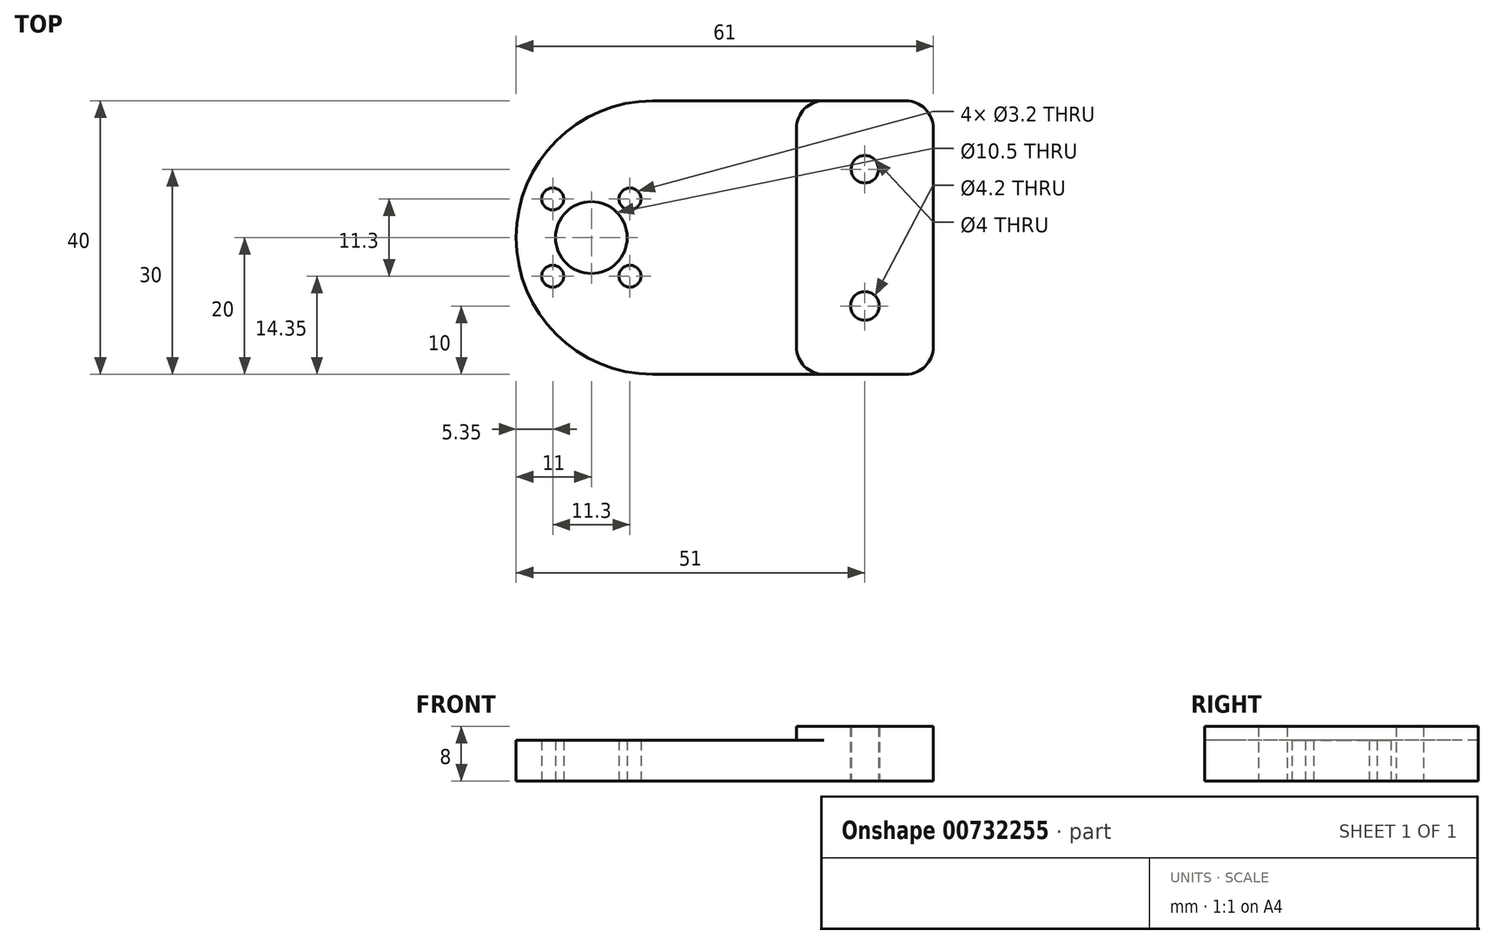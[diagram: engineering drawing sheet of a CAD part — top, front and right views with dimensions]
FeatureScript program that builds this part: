
annotation { "Feature Type Name" : "Feature", "Feature Type Description" : "" }
export const myFeature = defineFeature(function(context is Context, id is Id, definition is map)
    precondition{}
    {
        {
            var Q0;
            Q0=qCreatedBy(makeId("Top.planeOp"),FACE);
            var sketch = newSketch(context, id + "F0", { "sketchPlane" : qUnion([Q0])});
            skLineSegment(sketch, "E0.bottom", {"start": v(30.5, -20) * mm, "end": v(-30.5, -20) * mm});
            skLineSegment(sketch, "E0.top", {"start": v(30.5, 20) * mm, "end": v(-30.5, 20) * mm});
            skLineSegment(sketch, "E0.left", {"start": v(30.5, -20) * mm, "end": v(30.5, 20) * mm});
            skLineSegment(sketch, "E0.right", {"start": v(-30.5, -20) * mm, "end": v(-30.5, 20) * mm});
            skPoint(sketch, "E0.middle", {"position": v(0, 0) * mm});
            skCircle(sketch, "E1", {"center": v(-19.5, 0) * mm, "radius": 5.25 * mm});
            skLineSegment(sketch, "E2.bottom", {"start": v(-13.85, -5.65) * mm, "end": v(-25.15, -5.65) * mm, "construction": true});
            skLineSegment(sketch, "E2.top", {"start": v(-13.85, 5.65) * mm, "end": v(-25.15, 5.65) * mm, "construction": true});
            skLineSegment(sketch, "E2.left", {"start": v(-13.85, -5.65) * mm, "end": v(-13.85, 5.65) * mm, "construction": true});
            skLineSegment(sketch, "E2.right", {"start": v(-25.15, -5.65) * mm, "end": v(-25.15, 5.65) * mm, "construction": true});
            skCircle(sketch, "E3", {"center": v(-13.85, 5.65) * mm, "radius": 1.6 * mm});
            skCircle(sketch, "E4", {"center": v(-25.15, 5.65) * mm, "radius": 1.6 * mm});
            skCircle(sketch, "E5", {"center": v(-13.85, -5.65) * mm, "radius": 1.6 * mm});
            skCircle(sketch, "E6", {"center": v(-25.15, -5.65) * mm, "radius": 1.6 * mm});
            skCircle(sketch, "E7", {"center": v(20.5, -10) * mm, "radius": 2.1 * mm});
            skCircle(sketch, "E8", {"center": v(20.5, 10) * mm, "radius": 2 * mm});
            skSolve(sketch);
        }
        {
            var Q0;
            Q0=qSketchRegion(id+"F0",true);
            extrude(context, id + "F1", {"entities" : qUnion([Q0]), "depth" : 6 * mm, "offsetDistance" : 25 * mm});
        }
        {
            var Q0;
            Q0=qSketchRegion(id+"F0",true);
            extrude(context, id + "F2", {"entities" : qUnion([Q0]), "operationType" : NewBodyOperationType.REMOVE, "endBound" : BoundingType.THROUGH_ALL, "oppositeDirection" : true, "depth" : 25 * mm, "offsetDistance" : 25 * mm});
        }
        {
            var Q0;
            Q0=makeQuery(id+"F1.opExtrude","SWEPT_EDGE",EDGE,{"disambiguationData":[OSD([sQuery(id+"F0.wireOp",EDGE,"E0.bottom"),sQuery(id+"F0.wireOp",EDGE,"E0.right")])]});
            var Q1;
            Q1=makeQuery(id+"F1.opExtrude","SWEPT_EDGE",EDGE,{"disambiguationData":[OSD([sQuery(id+"F0.wireOp",EDGE,"E0.top"),sQuery(id+"F0.wireOp",EDGE,"E0.right")])]});
            fillet(context, id + "F3", {"entities" : qUnion([Q0, Q1]), "radius" : 20 * mm, "tangentPropagation" : true, "allowEdgeOverflow" : false});
        }
        {
            var Q0;
            Q0=makeQuery(id+"F1.opExtrude","CAP_FACE",FACE,{"disambiguationData":[OSD([sQuery(id+"F0.wireOp",EDGE,"E0.bottom"),sQuery(id+"F0.wireOp",EDGE,"E0.top"),sQuery(id+"F0.wireOp",EDGE,"E0.left"),sQuery(id+"F0.wireOp",EDGE,"E0.right"),sQuery(id+"F0.wireOp",EDGE,"E1"),sQuery(id+"F0.wireOp",EDGE,"E3"),sQuery(id+"F0.wireOp",EDGE,"E4"),sQuery(id+"F0.wireOp",EDGE,"E5"),sQuery(id+"F0.wireOp",EDGE,"E6"),sQuery(id+"F0.wireOp",EDGE,"E7"),sQuery(id+"F0.wireOp",EDGE,"E8")])],"isStart":false});
            var sketch = newSketch(context, id + "F4", { "sketchPlane" : qUnion([Q0])});
            skLineSegment(sketch, "E9.bottom", {"start": v(30.5, 20) * mm, "end": v(10.5, 20) * mm});
            skLineSegment(sketch, "E9.top", {"start": v(30.5, -20) * mm, "end": v(10.5, -20) * mm});
            skLineSegment(sketch, "E9.left", {"start": v(30.5, 20) * mm, "end": v(30.5, -20) * mm});
            skLineSegment(sketch, "E9.right", {"start": v(10.5, 20) * mm, "end": v(10.5, -20) * mm});
            skSolve(sketch);
        }
        {
            var Q0;
            Q0=makeQuery(id+"F4.imprint","IMPRINT",FACE,{"disambiguationData":[TD([[makeQuery(id+"F4.imprint","IMPRINT",EDGE,{"derivedFrom":sQuery(id+"F4.wireOp",EDGE,"E9.bottom")}),1.0]])]});
            extrude(context, id + "F5", {"entities" : qUnion([Q0]), "operationType" : NewBodyOperationType.ADD, "depth" : 2 * mm, "offsetDistance" : 25 * mm});
        }
        {
            var Q0;
            Q0=makeQuery(id+"F5.opExtrude","SWEPT_EDGE",EDGE,{"disambiguationData":[OSD([sQuery(id+"F0.wireOp",EDGE,"E0.bottom"),sQuery(id+"F4.wireOp",EDGE,"E9.top"),sQuery(id+"F4.wireOp",EDGE,"E9.right")])]});
            var Q1;
            Q1=makeQuery(id+"F5.boolean.opBoolean","MERGE",EDGE,{"derivedFrom":[makeQuery(id+"F1.opExtrude","SWEPT_EDGE",EDGE,{"disambiguationData":[OSD([sQuery(id+"F0.wireOp",EDGE,"E0.bottom"),sQuery(id+"F0.wireOp",EDGE,"E0.left")])]}),makeQuery(id+"F5.opExtrude","SWEPT_EDGE",EDGE,{"disambiguationData":[OSD([sQuery(id+"F4.wireOp",EDGE,"E9.top"),sQuery(id+"F4.wireOp",EDGE,"E9.left")])]})]});
            var Q2;
            Q2=makeQuery(id+"F5.opExtrude","SWEPT_EDGE",EDGE,{"disambiguationData":[OSD([sQuery(id+"F0.wireOp",EDGE,"E0.top"),sQuery(id+"F4.wireOp",EDGE,"E9.bottom"),sQuery(id+"F4.wireOp",EDGE,"E9.right")])]});
            var Q3;
            Q3=makeQuery(id+"F5.boolean.opBoolean","MERGE",EDGE,{"derivedFrom":[makeQuery(id+"F1.opExtrude","SWEPT_EDGE",EDGE,{"disambiguationData":[OSD([sQuery(id+"F0.wireOp",EDGE,"E0.top"),sQuery(id+"F0.wireOp",EDGE,"E0.left")])]}),makeQuery(id+"F5.opExtrude","SWEPT_EDGE",EDGE,{"disambiguationData":[OSD([sQuery(id+"F4.wireOp",EDGE,"E9.bottom"),sQuery(id+"F4.wireOp",EDGE,"E9.left")])]})]});
            fillet(context, id + "F6", {"entities" : qUnion([Q0, Q1, Q2, Q3]), "radius" : 4 * mm, "tangentPropagation" : true, "allowEdgeOverflow" : false});
        }
    });
